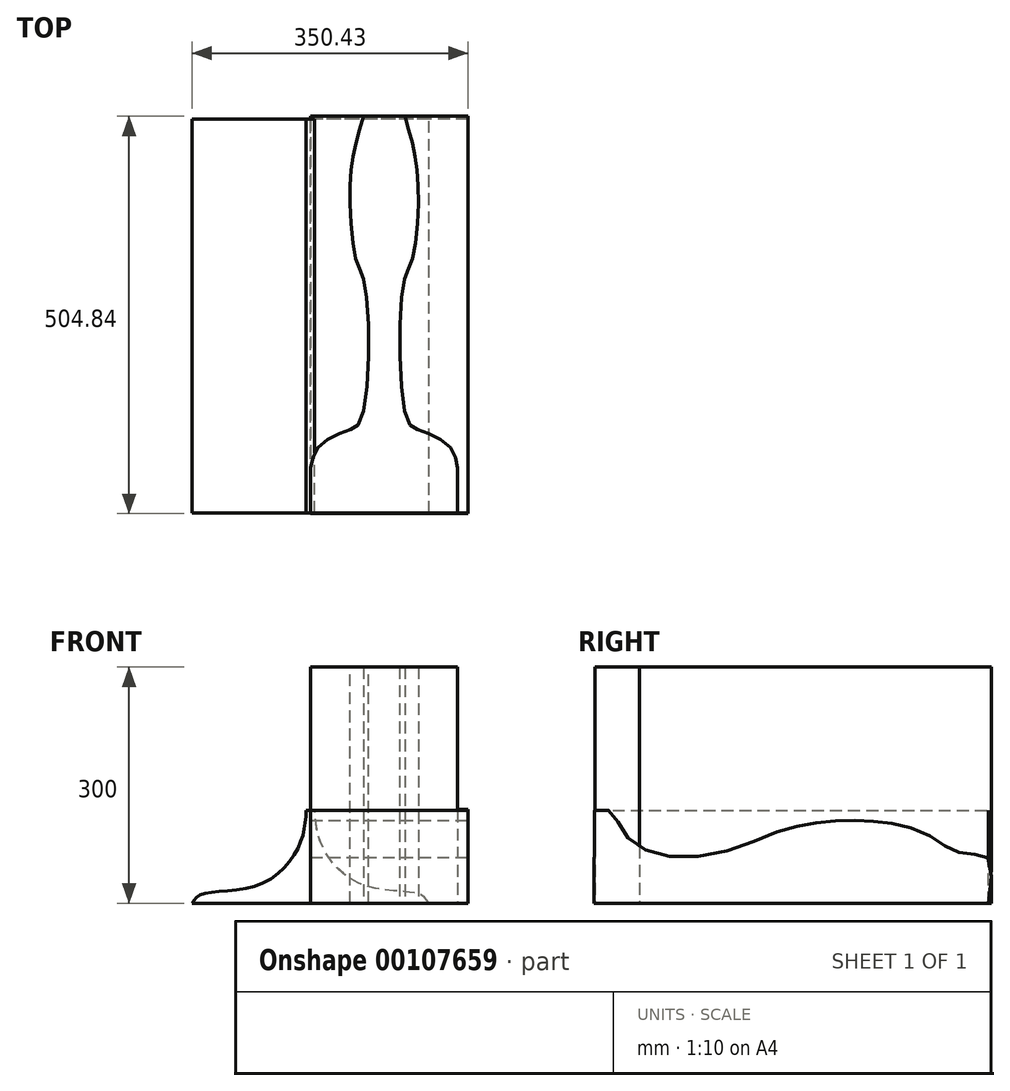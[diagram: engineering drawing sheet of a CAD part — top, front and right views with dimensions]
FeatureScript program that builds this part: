
annotation { "Feature Type Name" : "Feature", "Feature Type Description" : "" }
export const myFeature = defineFeature(function(context is Context, id is Id, definition is map)
    precondition{}
    {
        {
            var Q0;
            Q0=qCreatedBy(makeId("Front.planeOp"),FACE);
            var sketch = newSketch(context, id + "F0", { "sketchPlane" : qUnion([Q0])});
            skLineSegment(sketch, "E0", {"start": v(0, 0) * mm, "end": v(-150.43, 0) * mm});
            skFitSpline(sketch, "E1", {"points": [v(-150.43, 0) * mm, v(-138.01, 11.42) * mm, v(-65.9, 23.44) * mm, v(-14.22, 73.91) * mm, v(-5.4, 117.98) * mm], "startDerivative": vector(55.97, 90.12) * mm, "endDerivative": vector(12.51, 178.32) * mm});
            skLineSegment(sketch, "E2", {"start": v(-5.4, 117.98) * mm, "end": v(0, 117.98) * mm});
            skLineSegment(sketch, "E3", {"start": v(0, 117.98) * mm, "end": v(0, 0) * mm});
            skFitSpline(sketch, "E4.MirrorCS", {"points": [v(150.43, 0) * mm, v(138.01, 11.42) * mm, v(65.9, 23.44) * mm, v(14.22, 73.91) * mm, v(5.4, 117.98) * mm], "startDerivative": vector(-55.97, 90.12) * mm, "endDerivative": vector(-12.51, 178.32) * mm});
            skLineSegment(sketch, "E5", {"start": v(150.43, 0) * mm, "end": v(0, 0) * mm});
            skCircle(sketch, "E6", {"center": v(0, 31.05) * mm, "radius": 26.07 * mm});
            skLineSegment(sketch, "E7", {"start": v(5.4, 117.98) * mm, "end": v(0, 117.98) * mm});
            skSolve(sketch);
        }
        {
            var Q0;
            {var subQ5=sQuery(id+"F0.wireOp",EDGE,"E0");Q0=makeQuery(id+"F0.imprint","IMPRINT",FACE,{"disambiguationData":[TD([[makeQuery(id+"F0.imprint","IMPRINT",EDGE,{"derivedFrom":subQ5}),-1.0]])]});}
            var Q1;
            {var subQ0=sQuery(id+"F0.wireOp",EDGE,"E6");var subQ1=sQuery(id+"F0.wireOp",EDGE,"E3");var subQ2=makeQuery(id+"F0.imprint","INTERSECT",VERTEX,{"disambiguationData":[OD(0.0)],"derivedFrom":[subQ1,subQ0]});Q1=makeQuery(id+"F0.imprint","IMPRINT",FACE,{"disambiguationData":[TD([[makeQuery(id+"F0.imprint","IMPRINT",EDGE,{"disambiguationData":[TD([[subQ2,-1.0]])],"derivedFrom":subQ1}),1.0]])]});}
            var Q2;
            Q2=makeQuery(id+"F0.imprint","IMPRINT",FACE,{"disambiguationData":[TD([[makeQuery(id+"F0.imprint","IMPRINT",EDGE,{"derivedFrom":sQuery(id+"F0.wireOp",EDGE,"E4.MirrorCS")}),1.0]])]});
            var Q3;
            {var subQ0=sQuery(id+"F0.wireOp",EDGE,"E6");var subQ1=sQuery(id+"F0.wireOp",EDGE,"E3");var subQ2=makeQuery(id+"F0.imprint","INTERSECT",VERTEX,{"disambiguationData":[OD(0.0)],"derivedFrom":[subQ1,subQ0]});Q3=makeQuery(id+"F0.imprint","IMPRINT",FACE,{"disambiguationData":[TD([[makeQuery(id+"F0.imprint","IMPRINT",EDGE,{"disambiguationData":[TD([[subQ2,-1.0]])],"derivedFrom":subQ1}),-1.0]])]});}
            extrude(context, id + "F1", {"entities" : qUnion([Q0, Q1, Q2, Q3]), "endBound" : BoundingType.SYMMETRIC, "depth" : 500 * mm});
        }
        {
            var Q0;
            Q0=qCreatedBy(makeId("Right.planeOp"),FACE);
            var sketch = newSketch(context, id + "F2", { "sketchPlane" : qUnion([Q0])});
            skFitSpline(sketch, "E8", {"points": [v(-250.3, 117.73) * mm, v(-229.97, 117.1) * mm, v(-214.1, 91.05) * mm, v(-175.98, 64.37) * mm, v(-94.03, 63.1) * mm, v(-19.08, 90.41) * mm, v(22.4, 100.78) * mm, v(63.5, 105.02) * mm, v(101.68, 104.06) * mm, v(138.46, 99.3) * mm, v(179.75, 83.42) * mm, v(205.16, 66.9) * mm, v(231.84, 62.46) * mm, v(250.26, 56.75) * mm, v(250.26, 0) * mm], "startDerivative": vector(410.3, 79.32) * mm, "endDerivative": vector(-106.15, -779.43) * mm});
            skLineSegment(sketch, "E9", {"start": v(250.26, 0) * mm, "end": v(-250.94, 0) * mm});
            skLineSegment(sketch, "E10", {"start": v(-250.94, 0) * mm, "end": v(-250.3, 117.73) * mm});
            skSolve(sketch);
        }
        {
            var Q0;
            Q0 = qSketchRegion(id + "F2", true);
            extrude(context, id + "F3", {"entities" : qUnion([Q0]), "depth" : 200 * mm});
        }
        {
            var Q0;
            Q0=qCreatedBy(makeId("Top.planeOp"),FACE);
            var sketch = newSketch(context, id + "F4", { "sketchPlane" : qUnion([Q0])});
            skLineSegment(sketch, "E11", {"start": v(93.5, -252.9) * mm, "end": v(93.5, 253.89) * mm, "construction": true});
            skLineSegment(sketch, "E12", {"start": v(93.5, 253.89) * mm, "end": v(0, 253.89) * mm, "construction": true});
            skLineSegment(sketch, "E13", {"start": v(0, 253.89) * mm, "end": v(199.72, 253.89) * mm, "construction": true});
            skLineSegment(sketch, "E14", {"start": v(0, -249.86) * mm, "end": v(0, -193.21) * mm});
            skFitSpline(sketch, "E15", {"points": [v(0, -193.21) * mm, v(10.56, -165.9) * mm, v(45.97, -145.67) * mm, v(64.17, -131.5) * mm, v(69.23, 39.44) * mm, v(58.1, 70.8) * mm, v(50.01, 151.72) * mm, v(55.07, 208.37) * mm, v(67.2, 253.89) * mm], "startDerivative": vector(56.3, 314.92) * mm, "endDerivative": vector(116.2, 389.23) * mm});
            skLineSegment(sketch, "E16", {"start": v(67.2, 253.89) * mm, "end": v(93.5, 253.89) * mm});
            skLineSegment(sketch, "E17.MirrorCS", {"start": v(119.8, 253.89) * mm, "end": v(93.5, 253.89) * mm});
            skLineSegment(sketch, "E18.MirrorCS", {"start": v(93.5, 253.89) * mm, "end": v(187.02, 253.89) * mm, "construction": true});
            skLineSegment(sketch, "E19.MirrorCS", {"start": v(187.02, -249.86) * mm, "end": v(187.02, -193.21) * mm});
            skFitSpline(sketch, "E20.MirrorCS", {"points": [v(187.02, -193.21) * mm, v(176.45, -165.9) * mm, v(141.05, -145.67) * mm, v(122.84, -131.5) * mm, v(117.79, 39.44) * mm, v(128.91, 70.8) * mm, v(137, 151.72) * mm, v(131.95, 208.37) * mm, v(119.8, 253.89) * mm], "startDerivative": vector(-56.3, 314.92) * mm, "endDerivative": vector(-116.2, 389.23) * mm});
            skLineSegment(sketch, "E21", {"start": v(0, -249.86) * mm, "end": v(187.02, -249.86) * mm});
            skSolve(sketch);
        }
        {
            var Q0;
            Q0=makeQuery(id+"F4.imprint","IMPRINT",FACE,{"disambiguationData":[TD([[makeQuery(id+"F4.imprint","IMPRINT",EDGE,{"derivedFrom":sQuery(id+"F4.wireOp",EDGE,"E14")}),-1.0]])]});
            var Q1;
            Q1=sQuery(id+"F4.wireOp",EDGE,"E15");
            var Q2;
            Q2=sQuery(id+"F4.wireOp",EDGE,"E20.MirrorCS");
            var Q3;
            Q3=sQuery(id+"F4.wireOp",EDGE,"E19.MirrorCS");
            var Q4;
            Q4=sQuery(id+"F4.wireOp",EDGE,"E14");
            extrude(context, id + "F5", {"entities" : qUnion([Q0]), "surfaceEntities" : qUnion([Q1, Q2, Q3, Q4]), "depth" : 300 * mm});
        }
    });
